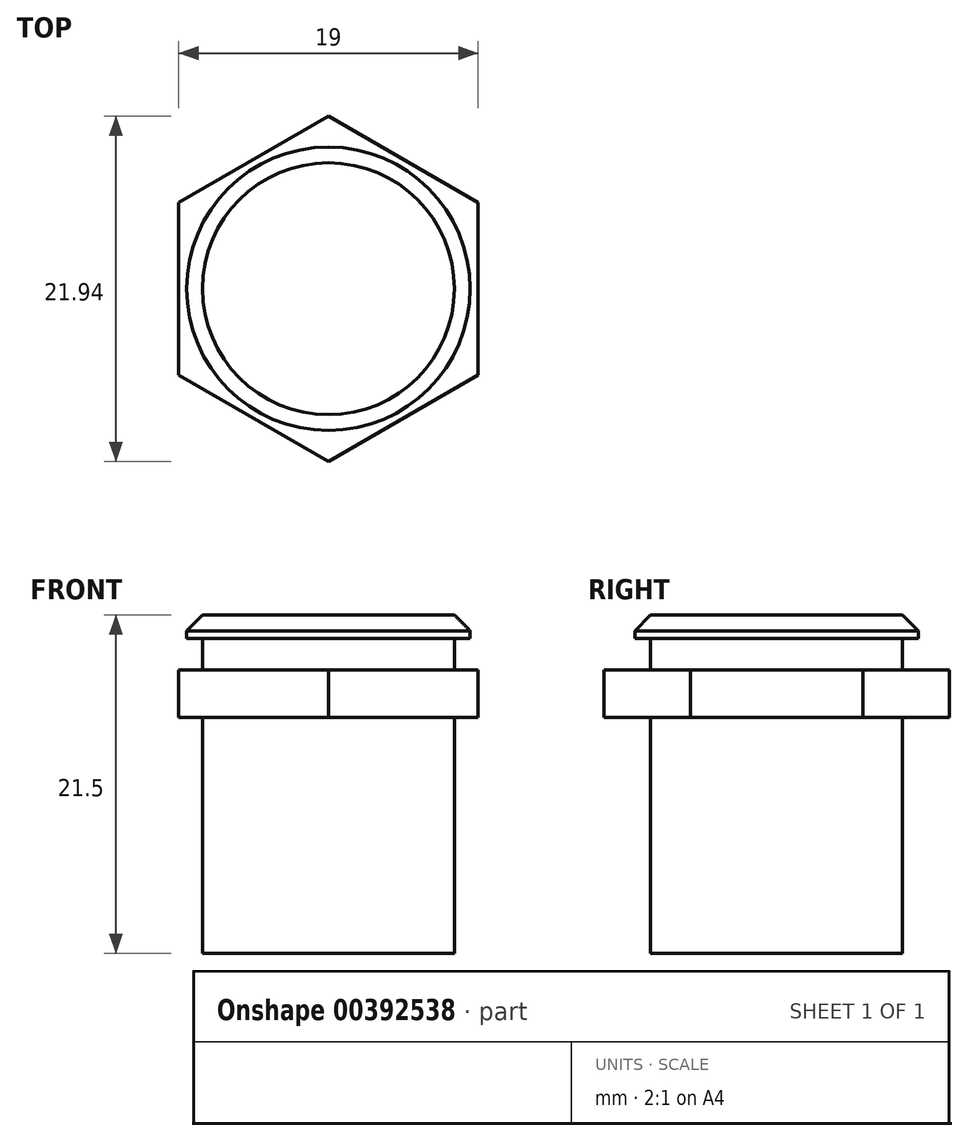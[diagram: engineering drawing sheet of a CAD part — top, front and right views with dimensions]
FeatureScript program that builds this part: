
annotation { "Feature Type Name" : "Feature", "Feature Type Description" : "" }
export const myFeature = defineFeature(function(context is Context, id is Id, definition is map)
    precondition{}
    {
        {
            var Q0;
            Q0=qCreatedBy(makeId("Top.planeOp"),FACE);
            var sketch = newSketch(context, id + "F0", { "sketchPlane" : qUnion([Q0])});
            skCircle(sketch, "E0", {"center": v(0, 0) * mm, "radius": 8 * mm});
            skCircle(sketch, "E1", {"center": v(0, 0) * mm, "radius": 9 * mm});
            skSolve(sketch);
        }
        {
            var Q0;
            Q0=makeQuery(id+"F0.imprint","IMPRINT",FACE,{"disambiguationData":[TD([[makeQuery(id+"F0.imprint","IMPRINT",EDGE,{"derivedFrom":sQuery(id+"F0.wireOp",EDGE,"E0")}),1.0]])]});
            extrude(context, id + "F1", {"entities" : qUnion([Q0]), "oppositeDirection" : true, "depth" : 20 * mm});
        }
        {
            var Q0;
            Q0=makeQuery(id+"F0.imprint","IMPRINT",FACE,{"disambiguationData":[TD([[makeQuery(id+"F0.imprint","IMPRINT",EDGE,{"derivedFrom":sQuery(id+"F0.wireOp",EDGE,"E0")}),-1.0]])]});
            var Q1;
            Q1=makeQuery(id+"F0.imprint","IMPRINT",FACE,{"disambiguationData":[TD([[makeQuery(id+"F0.imprint","IMPRINT",EDGE,{"derivedFrom":sQuery(id+"F0.wireOp",EDGE,"E0")}),1.0]])]});
            extrude(context, id + "F2", {"entities" : qUnion([Q0, Q1]), "operationType" : NewBodyOperationType.ADD, "depth" : 1.5 * mm});
        }
        {
            var Q0;
            Q0=makeQuery(id+"F2.opExtrude","CAP_EDGE",EDGE,{"disambiguationData":[OSD([sQuery(id+"F0.wireOp",EDGE,"E1")])],"isStart":false});
            chamfer(context, id + "F3", {"entities" : qUnion([Q0]), "width" : 1 * mm, "tangentPropagation" : true});
        }
        {
            var Q0;
            Q0=qCreatedBy(makeId("Top.planeOp"),FACE);
            cPlane(context, id + "F4", {"entities" : qUnion([Q0]), "cplaneType" : CPlaneType.OFFSET, "offset" : 2 * mm, "oppositeDirection" : true, "width" : 150 * mm, "height" : 150 * mm});
        }
        {
            var Q0;
            Q0=qCreatedBy(id+"F4.planeOp",FACE);
            var sketch = newSketch(context, id + "F5", { "sketchPlane" : qUnion([Q0])});
            skCircle(sketch, "E2.cCircle", {"center": v(0, 0) * mm, "radius": 10.97 * mm, "construction": true});
            skLineSegment(sketch, "E2.0", {"start": v(0, 10.97) * mm, "end": v(9.5, 5.48) * mm});
            skLineSegment(sketch, "E2.1", {"start": v(9.5, 5.48) * mm, "end": v(9.5, -5.48) * mm});
            skLineSegment(sketch, "E2.2", {"start": v(9.5, -5.48) * mm, "end": v(0, -10.97) * mm});
            skLineSegment(sketch, "E2.3", {"start": v(0, -10.97) * mm, "end": v(-9.5, -5.48) * mm});
            skLineSegment(sketch, "E2.4", {"start": v(-9.5, -5.48) * mm, "end": v(-9.5, 5.48) * mm});
            skLineSegment(sketch, "E2.5", {"start": v(-9.5, 5.48) * mm, "end": v(0, 10.97) * mm});
            skSolve(sketch);
        }
        {
            var Q0;
            Q0=makeQuery(id+"F5.imprint","IMPRINT",FACE,{"disambiguationData":[TD([[makeQuery(id+"F5.imprint","IMPRINT",EDGE,{"derivedFrom":sQuery(id+"F5.wireOp",EDGE,"E2.0")}),-1.0]])]});
            extrude(context, id + "F6", {"entities" : qUnion([Q0]), "operationType" : NewBodyOperationType.ADD, "oppositeDirection" : true, "depth" : 3 * mm});
        }
    });
